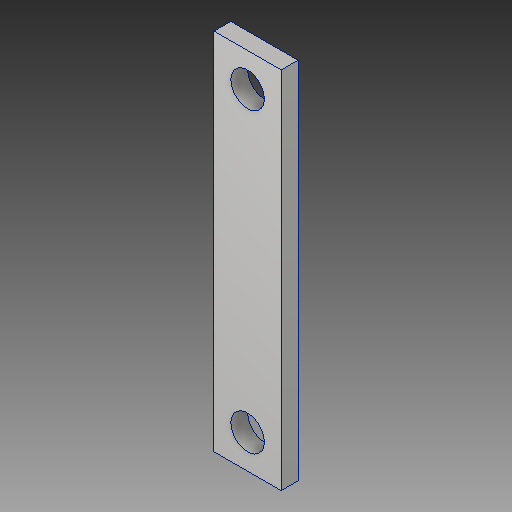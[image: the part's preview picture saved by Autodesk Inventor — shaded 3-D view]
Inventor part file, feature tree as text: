
AUTODESK INVENTOR PART (.ipt)
format: ipt  version: 2018.1 (Build 221171000, 171)  size: 103,936 bytes
history: native  units: mm
features: other x1, extrude x1, sketch x1
ambient origin geometry x8: Origin, YZ Plane, XZ Plane, XY Plane, X Axis, Y Axis, Z Axis, Center Point
bodies: Body1 (feature_tree)
feature tree (3):
  other  "ソリッド1"
  extrude  "押し出し1"  Depth=20.0mm
  sketch  "スケッチ1"
